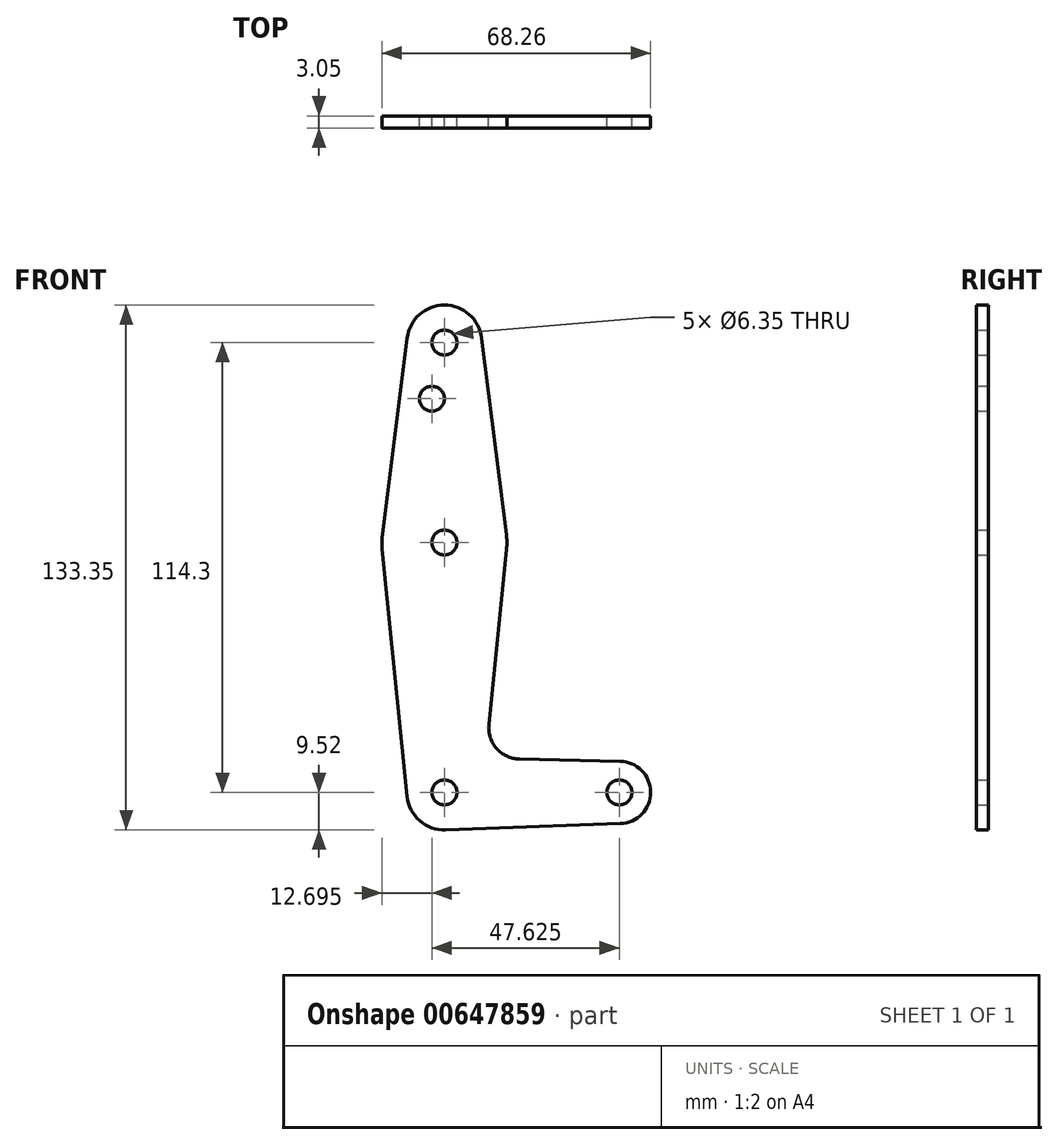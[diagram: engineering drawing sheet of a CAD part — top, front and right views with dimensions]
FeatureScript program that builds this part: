
annotation { "Feature Type Name" : "Feature", "Feature Type Description" : "" }
export const myFeature = defineFeature(function(context is Context, id is Id, definition is map)
    precondition{}
    {
        {
            var Q0;
            Q0=qCreatedBy(makeId("Front.planeOp"),FACE);
            var sketch = newSketch(context, id + "F0", { "sketchPlane" : qUnion([Q0])});
            skLineSegment(sketch, "E0", {"start": v(0, 0) * mm, "end": v(0, 114.3) * mm, "construction": true});
            skCircle(sketch, "E1", {"center": v(0, 114.3) * mm, "radius": 9.53 * mm});
            skCircle(sketch, "E2", {"center": v(0, 63.5) * mm, "radius": 15.88 * mm});
            skCircle(sketch, "E3", {"center": v(0, 0) * mm, "radius": 9.53 * mm});
            skLineSegment(sketch, "E4", {"start": v(0, 0) * mm, "end": v(44.45, 0) * mm, "construction": true});
            skCircle(sketch, "E5", {"center": v(44.45, 0) * mm, "radius": 7.94 * mm});
            skLineSegment(sketch, "E6", {"start": v(9.45, 115.5) * mm, "end": v(15.75, 65.48) * mm});
            skLineSegment(sketch, "E7", {"start": v(-9.45, 115.5) * mm, "end": v(-15.75, 65.48) * mm});
            skLineSegment(sketch, "E8", {"start": v(-15.8, 61.91) * mm, "end": v(-9.48, -0.95) * mm});
            skLineSegment(sketch, "E9", {"start": v(15.8, 61.91) * mm, "end": v(11.3, 17.23) * mm});
            skLineSegment(sketch, "E10", {"start": v(19.04, 8.49) * mm, "end": v(44.62, 7.94) * mm});
            skLineSegment(sketch, "E11", {"start": v(0.34, -9.52) * mm, "end": v(44.73, -7.93) * mm});
            skCircle(sketch, "E12", {"center": v(0, 114.3) * mm, "radius": 3.18 * mm});
            skCircle(sketch, "E13", {"center": v(-3.18, 100.03) * mm, "radius": 3.18 * mm});
            skCircle(sketch, "E14", {"center": v(0, 63.5) * mm, "radius": 3.18 * mm});
            skCircle(sketch, "E15", {"center": v(0, 0) * mm, "radius": 3.18 * mm});
            skCircle(sketch, "E16", {"center": v(44.45, 0) * mm, "radius": 3.18 * mm});
            skArc(sketch, "E17.filletArc", {"start": v(11.3, 17.23) * mm, "mid": v(13.26, 11.17) * mm, "end": v(19.04, 8.49) * mm});
            skSolve(sketch);
        }
        {
            var Q0;
            Q0=makeQuery(id+"F0.imprint","IMPRINT",FACE,{"disambiguationData":[TD([[makeQuery(id+"F0.imprint","IMPRINT",EDGE,{"derivedFrom":sQuery(id+"F0.wireOp",EDGE,"E15")}),-1.0]])]});
            var Q1;
            Q1=makeQuery(id+"F0.imprint","IMPRINT",FACE,{"disambiguationData":[TD([[makeQuery(id+"F0.imprint","IMPRINT",EDGE,{"derivedFrom":sQuery(id+"F0.wireOp",EDGE,"E16")}),-1.0]])]});
            var Q2;
            Q2=makeQuery(id+"F0.imprint","IMPRINT",FACE,{"disambiguationData":[TD([[makeQuery(id+"F0.imprint","IMPRINT",EDGE,{"derivedFrom":sQuery(id+"F0.wireOp",EDGE,"E14")}),-1.0]])]});
            var Q3;
            {var subQ3=sQuery(id+"F0.wireOp",EDGE,"E8");Q3=makeQuery(id+"F0.imprint","IMPRINT",FACE,{"disambiguationData":[TD([[makeQuery(id+"F0.imprint","IMPRINT",EDGE,{"derivedFrom":subQ3}),1.0]])]});}
            var Q4;
            {var subQ0=sQuery(id+"F0.wireOp",EDGE,"E6");Q4=makeQuery(id+"F0.imprint","IMPRINT",FACE,{"disambiguationData":[TD([[makeQuery(id+"F0.imprint","IMPRINT",EDGE,{"derivedFrom":subQ0}),-1.0]])]});}
            var Q5;
            Q5=makeQuery(id+"F0.imprint","IMPRINT",FACE,{"disambiguationData":[TD([[makeQuery(id+"F0.imprint","IMPRINT",EDGE,{"derivedFrom":sQuery(id+"F0.wireOp",EDGE,"E12")}),-1.0]])]});
            extrude(context, id + "F1", {"entities" : qUnion([Q0, Q1, Q2, Q3, Q4, Q5]), "depth" : 3.05 * mm, "offsetDistance" : 25.4 * mm});
        }
    });
